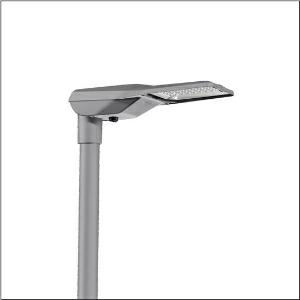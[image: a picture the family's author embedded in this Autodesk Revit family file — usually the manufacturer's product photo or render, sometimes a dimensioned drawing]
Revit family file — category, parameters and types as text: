
# Revit family: streetlight_sl_21_iq_mini___st1_0ab_5xe2m31u08jb_1fa0
name_source: partatom
category: Lighting Fixtures
units: mm (PartAtom-declared; Revit-internal decimal feet)

## family parameters
Cut with Voids When Loaded = No
Host = Face
Light Source = No
Part Type = Normal
Room Calculation Point = No
Round Connector Dimension = Use Diameter
Shared = No

## types (1)
- --- (1 x LED, 9870 lm, 72.5 W, 3000K)
    Apparent Load = 73 VA
    CIE Flux Codes = 40 74 97 100 100
    Color Rendering = 70
    Color Temperature = 3000K
    Default Elevation = 1800 mm
    Description = Streetlight SL 21 iQ mini, mast luminaire, primary light control with lens, of PMMA, primary optical cover: cover, of toughened safety glass, transparent, light distribution: ST1.0aB, light emission: direct distribution, primary light characteristic: asymmetric, installation type: post-top, side-entry, LED, High Power LED, rated luminous flux: 9.870lm, luminous efficacy: 136lm/W, light colour: 730, colour temperature: 3000K, control: presetting dimming logarithmic, Street-Remote, Auto-Match, Temp-Guard, Lumen-Switch, Night-Set, Smart-Wire, Light-Fading, Desk-Remote (wireless, voltage-free reading and setting of iQ features in the workshop via application-optimized NFC function/RFID function), optimised constant luminous flux control (CLO 2.0), mains connection: 220..240V, AC, 50/60Hz, start of lifetime: 73W, end of service life: 76W, reduction: 33W, luminaire housing, of diecast aluminium, powder-coated, Siteco® metallic grey (DB 702S), corrosivity category C5 mid according to DIN EN ISO 12944, please order mast flange separately, inclination adjustable: 0°, 5°, 10°, 15°, sealing non-destructively replaceable, multi-level sealing system, length: 628mm, width: 235mm, height: 110mm, mast flange for spigot size: 42mm (side-entry): 5XC10008XM4, 60/48mm (side-entry/post-top): 5XC10108XM2, 76/60mm (side-entry/post-top): 5XC10108XM1, Smart Interface below, protection rating (complete): IP66, insulation class (complete): insulation class II (safety insulation), certification: CE, ENEC, ENEC+, VDE, impact resistance: IK09, permissible operating ambient temperature for outdoor applications: -40..+50°C, standard-compliant lighting for roads and squares, packaging unit: 1 piece

Light Distribution: ST1.0aB
    Height = 110 mm
    Lamp = 1 x LED
    Lamp Light Flux = 9870 lm
    Lamp Power = 72.5 W
    Lamp count = 1
    Length = 625 mm
    Luminous efficacy = 136 lm/W
    Manufacturer = Siteco
    ModVariant = No
    Model = 5XE2M31U08JB
    Number of Poles = 1
    OnlyDefault = Yes
    Power Factor = 1
    Product Name = Streetlight SL 21 iQ mini | ST1.0aB
    Product group = mast luminaire | pylon top
    ProductGroupID = 6100
    Protection Class = Protection class II
    Protection Degree = IP 66
    RLX_Detail_Level = 1
    RLX_Emergency_Light_Flux = 0 lm
    RLX_Emergency_Type = 0
    RLX_Emergency_Type_DB = No
    RlxData = <blob elided: 92161 chars, md5=d6cd6036>
    Socket = socket
    Standby Power = 0 W
    System Light Flux = 9870 lm
    System Power = 73 W
    Type Comments = factory setting: luminous flux: 100 % | dim-lin: 254 | 755 mA
    Type Image = l_1003516.jpg
    URL = http://relux.com
    VarID = @adj_060489
    Voltage = 0 V
    Weight = 0.00 kg
    Width = 234 mm

## geometry (parser evidence)
native form markers: Blend x4, Sweep x10
no freeform markers — native parametric forms only
